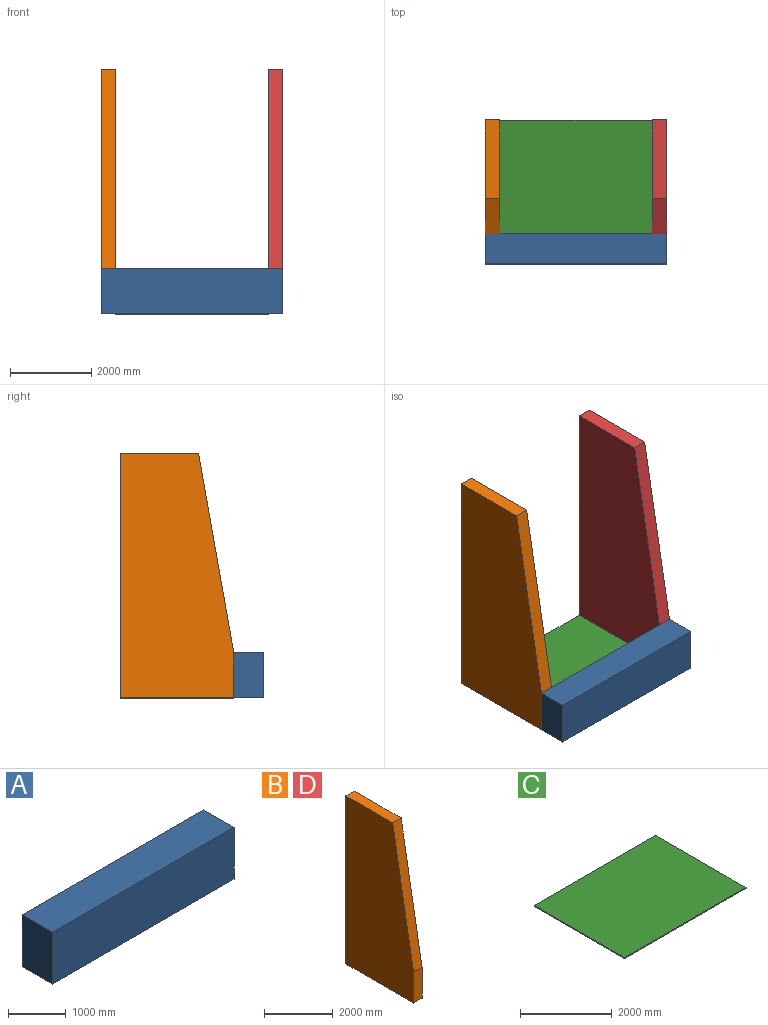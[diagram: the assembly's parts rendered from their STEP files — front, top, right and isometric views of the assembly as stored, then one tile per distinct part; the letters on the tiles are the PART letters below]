
ASSEMBLY  parts=4 mates=3
PART A: 6 faces, bbox 4450x740x1100 mm
  f0: plane 1100x740mm, normal (-1,0,0), area 814000mm2, adj f1,f3,f4,f5
  f1: plane 4450x1100mm, normal (0,-1,0), area 4895000mm2, adj f0,f2,f4,f5
  f2: plane 1100x740mm, normal (1,0,0), area 814000mm2, adj f1,f3,f4,f5
  f3: plane 4450x1100mm, normal (0,1,0), area 4895000mm2, adj f0,f2,f4,f5
  f4: plane 4450x740mm, normal (0,0,1), area 3293000mm2, adj f0,f1,f2,f3
  f5: plane 4450x740mm, normal (0,0,-1), area 3293000mm2, adj f0,f1,f2,f3
PART B: 7 faces, bbox 350x2790x6000 mm
  f0: plane 2790x350mm, normal (0,0,-1), area 976500mm2, adj f1,f4,f5,f6
  f1: plane 6000x350mm, normal (0,1,0), area 2100000mm2, adj f0,f2,f5,f6
  f2: plane 1926x350mm, normal (0,0,1), area 674099.2mm2, adj f1,f3,f5,f6
  f3: plane 4900x864mm, normal (0,-0.98,0.17), area 1741456.6mm2, adj f2,f4,f5,f6
  f4: plane 1100x350mm, normal (0,-1,0), area 385000mm2, adj f0,f3,f5,f6
  f5: plane 6000x2790mm, normal (1,0,0), area 14623194.6mm2, adj f0,f1,f2,f3,f4
  f6: plane 6000x2790mm, normal (-1,0,0), area 14623194.6mm2, adj f0,f1,f2,f3,f4
PART C: 6 faces, bbox 3750x2790x25 mm
  f0: plane 2790x25mm, normal (-1,0,0), area 69750mm2, adj f1,f3,f4,f5
  f1: plane 3750x25mm, normal (0,-1,0), area 93750mm2, adj f0,f2,f4,f5
  f2: plane 2790x25mm, normal (1,0,0), area 69750mm2, adj f1,f3,f4,f5
  f3: plane 3750x25mm, normal (0,1,0), area 93750mm2, adj f0,f2,f4,f5
  f4: plane 3750x2790mm, normal (0,0,-1), area 10462500mm2, adj f0,f1,f2,f3
  f5: plane 3750x2790mm, normal (0,0,1), area 10462500mm2, adj f0,f1,f2,f3
PART D: same geometry as B
PLACE A t=(-300.87,-858.63,265.47)mm
PLACE B t=(-300.87,-118.63,265.47)mm
PLACE C t=(49.13,-118.63,265.47)mm
PLACE D t=(3799.13,-118.63,265.47)mm
MATE fastened A.f5 <-> C.f5  axis (0,0,-1) through (1924.13,-118.63,265.47)mm
MATE fastened D.f4 <-> A.f3  axis (0,-1,0) through (4149.13,-118.63,815.47)mm
MATE fastened B.f4 <-> A.f3  axis (0,-1,0) through (-300.87,-118.63,815.47)mm
